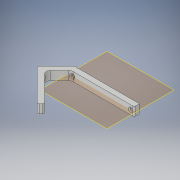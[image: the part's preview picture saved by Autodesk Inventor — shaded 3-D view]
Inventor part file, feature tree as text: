
AUTODESK INVENTOR PART (.ipt)
format: ipt  version: 2019 (Build 230136000, 136)  size: 214,528 bytes
history: native  units: mm
features: fillet x5, sketch x3, extrude x3, chamfer x2, plane x1
ambient origin geometry x8: Origin, YZ Plane, XZ Plane, XY Plane, X Axis, Y Axis, Z Axis, Center Point
bodies: Solid1 (feature_tree)
feature tree (14):
  sketch  "Sketch1"  dims[d0=66.0mm d1=90.0mm d2=3.4mm d3=3.4mm d4=45.0mm d5=37.0mm d6=37.0mm]
  plane  "Work Plane1"
  extrude  "Extrusion1"  Depth=90.0mm
  fillet  "Fillet1"  Radius=3.4mm
  fillet  "Fillet2"  Radius=3.4mm
  fillet  "Fillet3"  Radius=45.0mm
  fillet  "Fillet4"  Radius=37.0mm
  fillet  "Fillet5"  Radius=37.0mm
  extrude  "Extrusion2"  TaperAngle=135.0deg  [1 undecoded]
  extrude  "Extrusion3"  TaperAngle=135.0deg  [1 undecoded]
  chamfer  "Chamfer1"  Angle=45.0deg  [1 undecoded]
  chamfer  "Chamfer2"  Distance=6.0mm
  sketch  "Sketch2"  dims[d7=30.0mm d8=135.0deg]
  sketch  "Sketch3"  dims[d9=100.0mm d10=135.0deg d11=45.0deg d13=6.0mm d14=6.0mm d15=135.0deg d16=14.451339mm d17=6.0mm d18=20.162951mm d19=15.213203mm d20=10.0mm d21=0.0mm d22=5.0mm d23=0.5mm d24=2.0mm d25=2.0mm d26=2.0mm d27=10.0mm d28=0.0mm d29=180.0deg d30=30.0mm d31=3.5mm d32=3.5mm d33=10.0mm d34=0.0mm d35=1.0mm d36=2.0mm d37=45.0deg d38=1.0mm d39=2.0mm d40=45.0deg]
note: 3 required parameter values undecoded (feature->parameter linkage not recoverable at this tier; creation-order binding heuristic only, values carry confidence <= 0.55)
